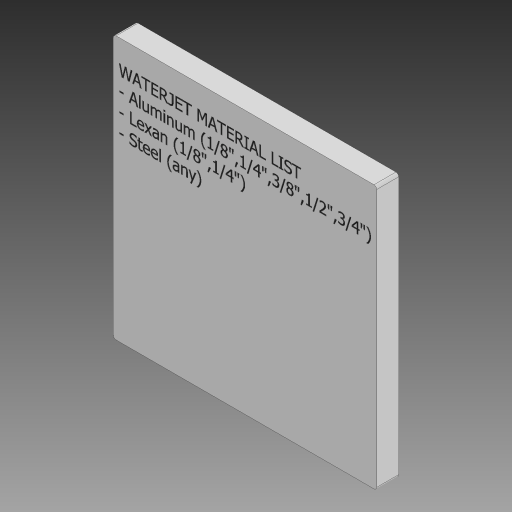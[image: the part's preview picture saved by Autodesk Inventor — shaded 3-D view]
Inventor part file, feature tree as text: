
AUTODESK INVENTOR PART (.ipt)
format: ipt  version: 2023.4 (Build 274418000, 418)  size: 1,406,976 bytes
history: native  units: in
note: dims shown in document units (in); Inventor stores cm internally (conversion verified against a paired STEP export)
features: sketch x2, extrude x1, emboss x1, fillet x1
ambient origin geometry x8: Origin, YZ Plane, XZ Plane, XY Plane, X Axis, Y Axis, Z Axis, Center Point
bodies: Solid1 (feature_tree)
feature tree (5):
  extrude  "Extrusion1"  Depth=12.0in
  emboss  "Emboss1"
  fillet  "Fillet1"  Radius=1.0in
  sketch  "Sketch1"  dims[d0=12.0in d1=12.0in d2=1.0in d3=0.0in]
  sketch  "Sketch2"  dims[d4=1.0in d5=0.25in d6=0.01in d7=0.0in d8=0.125in]
